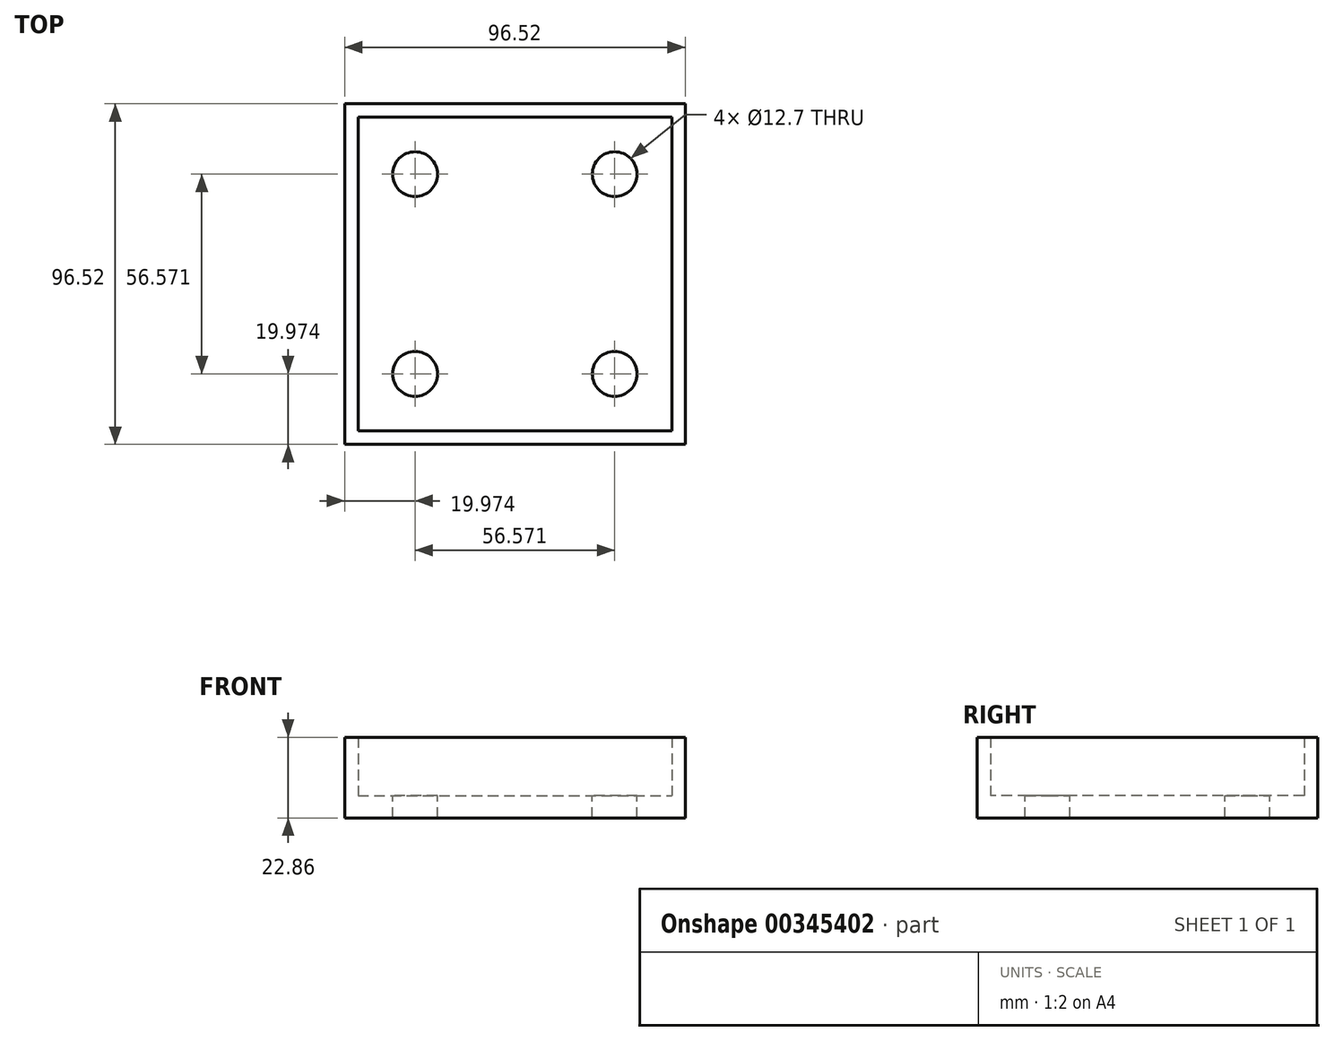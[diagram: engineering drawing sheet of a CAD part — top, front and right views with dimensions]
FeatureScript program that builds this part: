
annotation { "Feature Type Name" : "Feature", "Feature Type Description" : "" }
export const myFeature = defineFeature(function(context is Context, id is Id, definition is map)
    precondition{}
    {
        {
            var Q0;
            Q0=qCreatedBy(makeId("Top.planeOp"),FACE);
            var sketch = newSketch(context, id + "F0", { "sketchPlane" : qUnion([Q0])});
            skLineSegment(sketch, "E0.bottom", {"start": v(0, 0) * mm, "end": v(96.52, 0) * mm});
            skLineSegment(sketch, "E0.top", {"start": v(0, 96.52) * mm, "end": v(96.52, 96.52) * mm});
            skLineSegment(sketch, "E0.left", {"start": v(0, 0) * mm, "end": v(0, 96.52) * mm});
            skLineSegment(sketch, "E0.right", {"start": v(96.52, 0) * mm, "end": v(96.52, 96.52) * mm});
            skSolve(sketch);
        }
        {
            var Q0;
            Q0=qSketchRegion(id+"F0",true);
            extrude(context, id + "F1", {"entities" : qUnion([Q0]), "depth" : 6.35 * mm});
        }
        {
            var Q0;
            Q0=makeQuery(id+"F1.opExtrude","CAP_FACE",FACE,{"disambiguationData":[OSD([sQuery(id+"F0.wireOp",EDGE,"E0.bottom"),sQuery(id+"F0.wireOp",EDGE,"E0.top"),sQuery(id+"F0.wireOp",EDGE,"E0.left"),sQuery(id+"F0.wireOp",EDGE,"E0.right")])],"isStart":false});
            var sketch = newSketch(context, id + "F2", { "sketchPlane" : qUnion([Q0])});
            skLineSegment(sketch, "E1.bottom", {"start": v(0, 96.52) * mm, "end": v(96.52, 96.52) * mm});
            skLineSegment(sketch, "E1.top", {"start": v(0, 0) * mm, "end": v(96.52, 0) * mm});
            skLineSegment(sketch, "E1.left", {"start": v(0, 96.52) * mm, "end": v(0, 0) * mm});
            skLineSegment(sketch, "E1.right", {"start": v(96.52, 96.52) * mm, "end": v(96.52, 0) * mm});
            skLineSegment(sketch, "E2.bottom", {"start": v(3.81, 92.71) * mm, "end": v(92.71, 92.71) * mm});
            skLineSegment(sketch, "E2.top", {"start": v(3.81, 3.81) * mm, "end": v(92.71, 3.81) * mm});
            skLineSegment(sketch, "E2.left", {"start": v(3.81, 92.71) * mm, "end": v(3.81, 3.81) * mm});
            skLineSegment(sketch, "E2.right", {"start": v(92.71, 92.71) * mm, "end": v(92.71, 3.81) * mm});
            skSolve(sketch);
        }
        {
            var Q0;
            Q0=qSketchRegion(id+"F2",true);
            extrude(context, id + "F3", {"entities" : qUnion([Q0]), "operationType" : NewBodyOperationType.ADD, "depth" : 16.5 * mm});
        }
        {
            var Q0;
            Q0=makeQuery(id+"F1.opExtrude","CAP_FACE",FACE,{"disambiguationData":[OSD([sQuery(id+"F0.wireOp",EDGE,"E0.bottom"),sQuery(id+"F0.wireOp",EDGE,"E0.top"),sQuery(id+"F0.wireOp",EDGE,"E0.left"),sQuery(id+"F0.wireOp",EDGE,"E0.right")])],"isStart":false});
            var sketch = newSketch(context, id + "F4", { "sketchPlane" : qUnion([Q0])});
            skLineSegment(sketch, "E3", {"start": v(3.8, 92.71) * mm, "end": v(92.71, 3.8) * mm, "construction": true});
            skLineSegment(sketch, "E4", {"start": v(3.8, 3.8) * mm, "end": v(92.71, 92.71) * mm, "construction": true});
            skCircle(sketch, "E5", {"center": v(19.97, 76.55) * mm, "radius": 6.35 * mm});
            skLineSegment(sketch, "E6", {"start": v(3.81, 48.26) * mm, "end": v(92.71, 48.26) * mm, "construction": true});
            skCircle(sketch, "E7.MirrorC", {"center": v(19.97, 19.97) * mm, "radius": 6.35 * mm});
            skLineSegment(sketch, "E8", {"start": v(48.26, 92.71) * mm, "end": v(48.26, 3.8) * mm, "construction": true});
            skCircle(sketch, "E9.MirrorC", {"center": v(76.55, 19.97) * mm, "radius": 6.35 * mm});
            skCircle(sketch, "E10.MirrorC", {"center": v(76.55, 76.55) * mm, "radius": 6.35 * mm});
            skSolve(sketch);
        }
        {
            var Q0;
            Q0=qSketchRegion(id+"F4",true);
            extrude(context, id + "F5", {"entities" : qUnion([Q0]), "operationType" : NewBodyOperationType.REMOVE, "endBound" : BoundingType.THROUGH_ALL, "oppositeDirection" : true, "depth" : 25.4 * mm});
        }
    });
